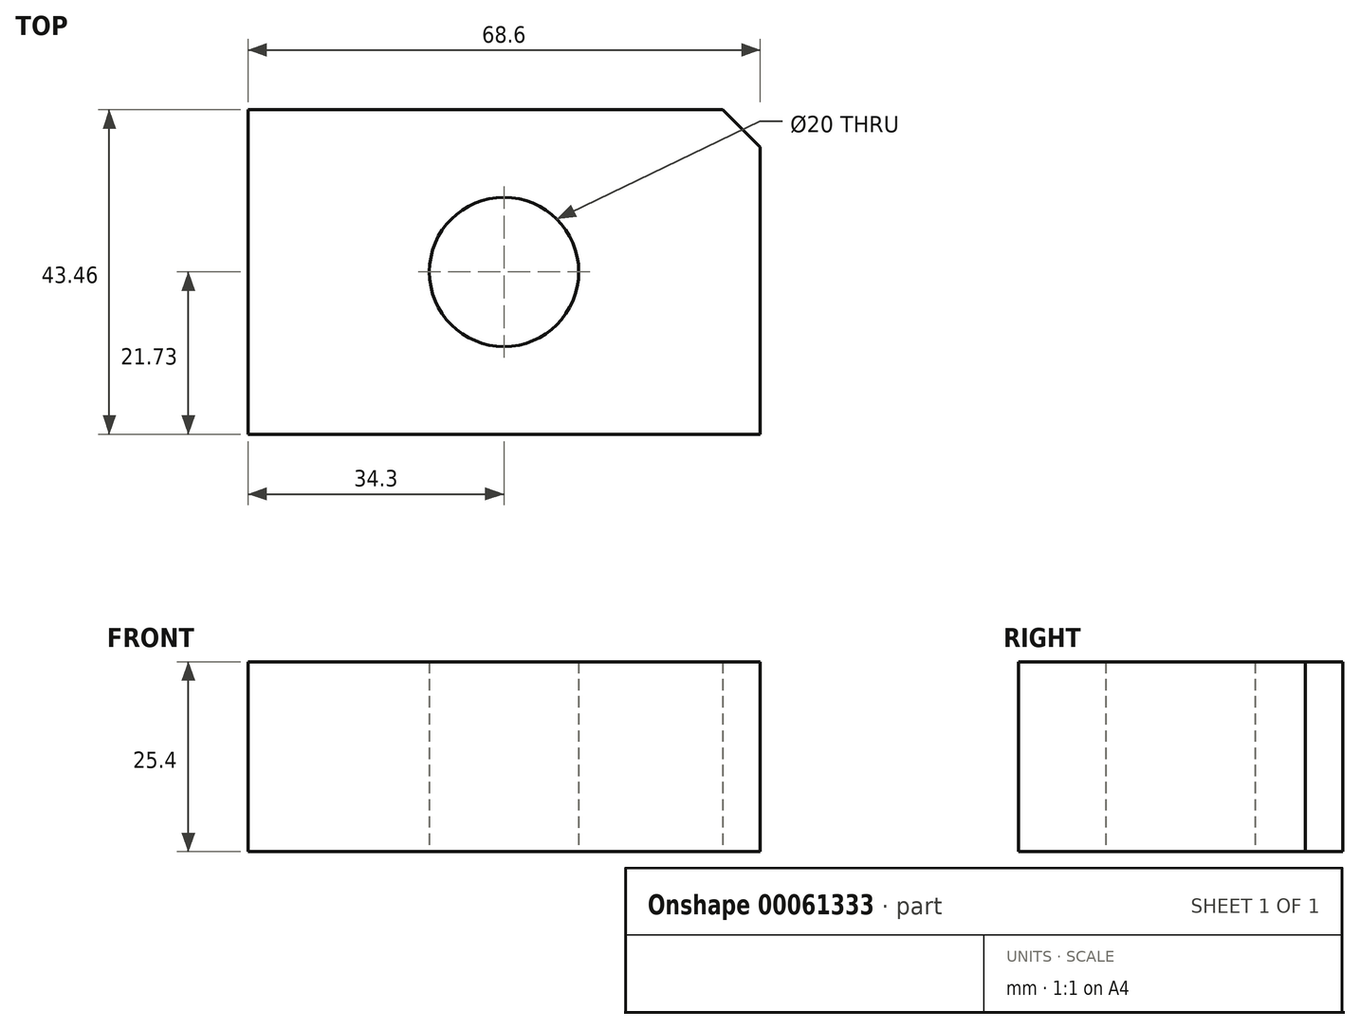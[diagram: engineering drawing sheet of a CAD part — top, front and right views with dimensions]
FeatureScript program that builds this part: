
annotation { "Feature Type Name" : "Feature", "Feature Type Description" : "" }
export const myFeature = defineFeature(function(context is Context, id is Id, definition is map)
    precondition{}
    {
        {
            var Q0;
            Q0=qCreatedBy(makeId("Top.planeOp"),FACE);
            var sketch = newSketch(context, id + "F0", { "sketchPlane" : qUnion([Q0])});
            skLineSegment(sketch, "E0.rect.bottom", {"start": v(34.3, -21.73) * mm, "end": v(-34.3, -21.73) * mm});
            skLineSegment(sketch, "E0.rect.top", {"start": v(34.3, 21.73) * mm, "end": v(-34.3, 21.73) * mm});
            skLineSegment(sketch, "E0.rect.left", {"start": v(34.3, -21.73) * mm, "end": v(34.3, 21.73) * mm});
            skLineSegment(sketch, "E0.rect.right", {"start": v(-34.3, -21.73) * mm, "end": v(-34.3, 21.73) * mm});
            skPoint(sketch, "E0.rect.middle", {"position": v(0, 0) * mm});
            skSolve(sketch);
        }
        {
            var Q0;
            Q0=makeQuery(id+"F0.imprint","IMPRINT",FACE,{"disambiguationData":[TD([[makeQuery(id+"F0.imprint","IMPRINT",EDGE,{"derivedFrom":sQuery(id+"F0.wireOp",EDGE,"E0.rect.bottom")}),-1.0]])]});
            extrude(context, id + "F1", {"entities" : qUnion([Q0]), "depth" : 25.4 * mm});
        }
        {
            var Q0;
            Q0=sQuery(id+"F0.wireOp",VERTEX,"E0.rect.middle");
            var Q1;
            Q1=makeQuery(id+"F1.opExtrude","SWEPT_BODY",BODY,{"disambiguationData":[OSD([sQuery(id+"F0.wireOp",EDGE,"E0.rect.bottom"),sQuery(id+"F0.wireOp",EDGE,"E0.rect.top"),sQuery(id+"F0.wireOp",EDGE,"E0.rect.left"),sQuery(id+"F0.wireOp",EDGE,"E0.rect.right")])]});
            hole(context, id + "F2", {"style" : HoleStyle.SIMPLE, "holeDiameter" : 5 * mm, "endStyle" : HoleEndStyle.THROUGH, "oppositeDirection" : true, "locations" : qUnion([Q0]), "scope" : qUnion([Q1])});
        }
        {
            var Q0;
            Q0=makeQuery(id+"F0.imprint","IMPRINT",FACE,{"disambiguationData":[TD([[makeQuery(id+"F0.imprint","IMPRINT",EDGE,{"derivedFrom":sQuery(id+"F0.wireOp",EDGE,"E0.rect.bottom")}),-1.0]])]});
            var sketch = newSketch(context, id + "F3", { "sketchPlane" : qUnion([Q0])});
            skCircle(sketch, "E1", {"center": v(0, 0) * mm, "radius": 10 * mm});
            skSolve(sketch);
        }
        {
            var Q0;
            Q0 = qSketchRegion(id + "F3", true);
            extrude(context, id + "F4", {"entities" : qUnion([Q0]), "operationType" : NewBodyOperationType.REMOVE, "endBound" : BoundingType.THROUGH_ALL, "depth" : 25 * mm});
        }
        {
            var Q0;
            Q0=makeQuery(id+"F1.opExtrude","SWEPT_EDGE",EDGE,{"disambiguationData":[OSD([sQuery(id+"F0.wireOp",EDGE,"E0.rect.top"),sQuery(id+"F0.wireOp",EDGE,"E0.rect.left")])]});
            chamfer(context, id + "F5", {"entities" : qUnion([Q0]), "width" : 5 * mm, "tangentPropagation" : true});
        }
    });
